annotation { "Feature Type Name" : "Feature", "Feature Type Description" : "" }
export const myFeature = defineFeature(function(context is Context, id is Id, definition is map)
    precondition{}
    {
        {
            var Q0;
            Q0=qCreatedBy(makeId("Top.planeOp"),FACE);
            var sketch = newSketch(context, id + "F0", { "sketchPlane" : qUnion([Q0])});
            skLineSegment(sketch, "E0.bottom", {"start": v(-32.74, 11.83) * mm, "end": v(23.8, 11.83) * mm});
            skLineSegment(sketch, "E0.top", {"start": v(-31.9, -12.45) * mm, "end": v(24.42, -12.45) * mm});
            skLineSegment(sketch, "E1", {"start": v(23.8, 11.83) * mm, "end": v(117.26, 11.83) * mm});
            skLineSegment(sketch, "E2", {"start": v(24.42, -12.45) * mm, "end": v(117.26, -12.45) * mm});
            skLineSegment(sketch, "E3.top", {"start": v(39.01, 6.27) * mm, "end": v(-19.73, 6.27) * mm});
            skLineSegment(sketch, "E4", {"start": v(-32.74, 6.27) * mm, "end": v(117.26, 6.27) * mm});
            skLineSegment(sketch, "E5", {"start": v(117.26, 6.27) * mm, "end": v(117.26, 1.82) * mm});
            skLineSegment(sketch, "E6", {"start": v(-32.74, 6.27) * mm, "end": v(-32.74, 1.82) * mm});
            skLineSegment(sketch, "E7", {"start": v(-32.74, 1.82) * mm, "end": v(117.26, 1.82) * mm});
            skArc(sketch, "E8", {"start": v(-32.74, 11.83) * mm, "mid": v(-44.04, -0.72) * mm, "end": v(-31.9, -12.45) * mm});
            skPoint(sketch, "E9.end.orphan", {"position": v(-36.76, -10.55) * mm});
            skArc(sketch, "E10", {"start": v(117.26, -12.45) * mm, "mid": v(129.4, -0.31) * mm, "end": v(117.26, 11.83) * mm});
            skText(sketch, "E11", { "text": "Rocket League", "fontName": "OpenSans-Bold.ttf"});
            skText(sketch, "E12", { "text": "Break-out Type S", "fontName": "OpenSans-Italic.ttf"});
            const initialGuessF0  = {"E11": [-0.0319, -0.00636, 1, 0, 0.00607], "E12": [0.03122, -0.01078, 1, 0, 0.00442]};
            skSetInitialGuess(sketch, initialGuessF0);
            skSolve(sketch);
        }
        {
            var Q0;
            Q0=makeQuery(id+"F0.imprint","IMPRINT",FACE,{"disambiguationData":[TD([[makeQuery(id+"F0.imprint","IMPRINT",EDGE,{"derivedFrom":sQuery(id+"F0.wireOp",EDGE,"E0.bottom")}),-1.0]])]});
            extrude(context, id + "F1", {"entities" : qUnion([Q0]), "depth" : 4.2 * mm, "offsetDistance" : 25 * mm});
        }
    });